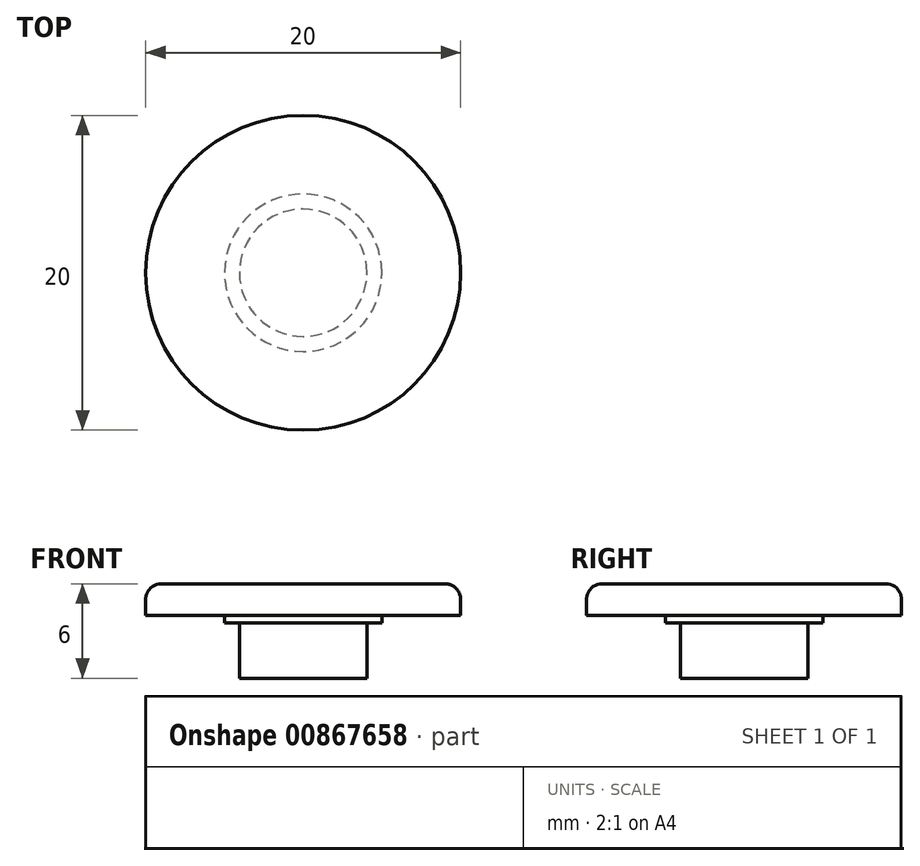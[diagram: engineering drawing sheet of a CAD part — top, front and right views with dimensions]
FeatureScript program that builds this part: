
annotation { "Feature Type Name" : "Feature", "Feature Type Description" : "" }
export const myFeature = defineFeature(function(context is Context, id is Id, definition is map)
    precondition{}
    {
        {
            var Q0;
            Q0=qCreatedBy(makeId("Top.planeOp"),FACE);
            var sketch = newSketch(context, id + "F0", { "sketchPlane" : qUnion([Q0])});
            skCircle(sketch, "E0", {"center": v(0, 0) * mm, "radius": 10 * mm});
            skCircle(sketch, "E1", {"center": v(0, 0) * mm, "radius": 4.05 * mm});
            skCircle(sketch, "E2", {"center": v(0, 0) * mm, "radius": 5 * mm});
            skSolve(sketch);
        }
        {
            var Q0;
            Q0=makeQuery(id+"F0.imprint","IMPRINT",FACE,{"disambiguationData":[TD([[makeQuery(id+"F0.imprint","IMPRINT",EDGE,{"derivedFrom":sQuery(id+"F0.wireOp",EDGE,"E1")}),1.0]])]});
            extrude(context, id + "F1", {"entities" : qUnion([Q0]), "oppositeDirection" : true, "depth" : 6 * mm, "offsetDistance" : 25 * mm});
        }
        {
            var Q0;
            Q0=makeQuery(id+"F0.imprint","IMPRINT",FACE,{"disambiguationData":[TD([[makeQuery(id+"F0.imprint","IMPRINT",EDGE,{"derivedFrom":sQuery(id+"F0.wireOp",EDGE,"E1")}),-1.0]])]});
            extrude(context, id + "F2", {"entities" : qUnion([Q0]), "operationType" : NewBodyOperationType.ADD, "oppositeDirection" : true, "depth" : 2.5 * mm, "offsetDistance" : 25 * mm});
        }
        {
            var Q0;
            Q0=makeQuery(id+"F0.imprint","IMPRINT",FACE,{"disambiguationData":[TD([[makeQuery(id+"F0.imprint","IMPRINT",EDGE,{"derivedFrom":sQuery(id+"F0.wireOp",EDGE,"E0")}),1.0]])]});
            extrude(context, id + "F3", {"entities" : qUnion([Q0]), "operationType" : NewBodyOperationType.ADD, "oppositeDirection" : true, "depth" : 2 * mm, "offsetDistance" : 25 * mm});
        }
        {
            var Q0;
            Q0=makeQuery(id+"F3.opExtrude","CAP_EDGE",EDGE,{"disambiguationData":[OSD([sQuery(id+"F0.wireOp",EDGE,"E0")])],"isStart":true});
            fillet(context, id + "F4", {"entities" : qUnion([Q0]), "radius" : 1 * mm, "tangentPropagation" : true, "allowEdgeOverflow" : false});
        }
    });
